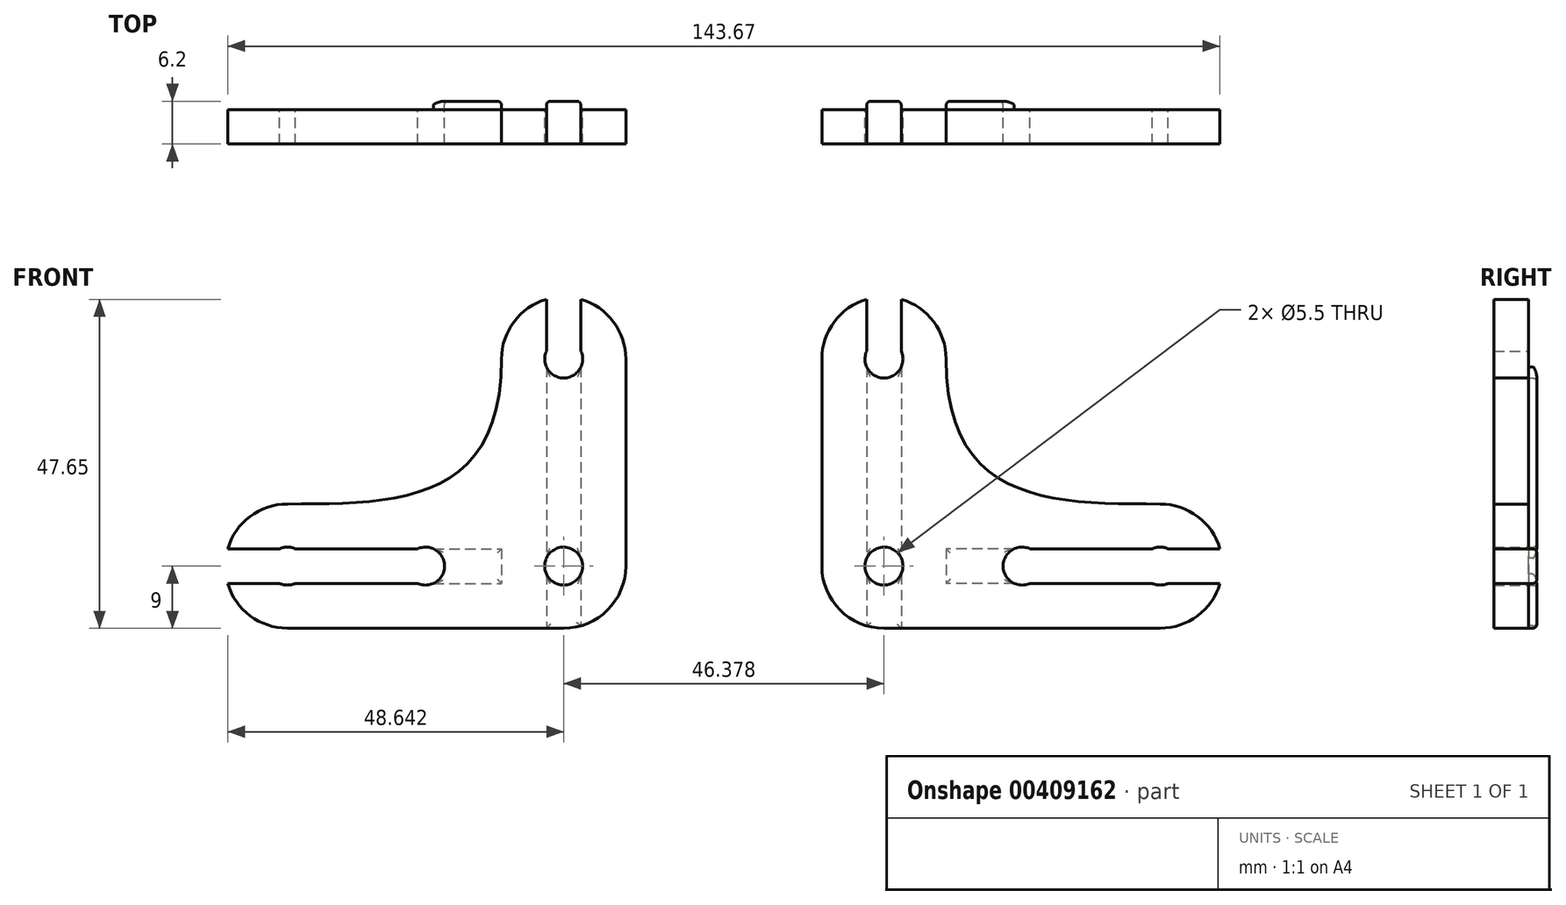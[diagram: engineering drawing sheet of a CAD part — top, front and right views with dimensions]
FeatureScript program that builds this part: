
annotation { "Feature Type Name" : "Feature", "Feature Type Description" : "" }
export const myFeature = defineFeature(function(context is Context, id is Id, definition is map)
    precondition{}
    {
        {
            var Q0;
            Q0=qCreatedBy(makeId("Front.planeOp"),FACE);
            var sketch = newSketch(context, id + "F0", { "sketchPlane" : qUnion([Q0])});
            skLineSegment(sketch, "E0.left", {"start": v(-18, 0) * mm, "end": v(-18, 30) * mm});
            skArc(sketch, "E1", {"start": v(-18, 30) * mm, "mid": v(-9, 39) * mm, "end": v(0, 30) * mm});
            skArc(sketch, "E2", {"start": v(31, 9) * mm, "mid": v(37.36, 6.36) * mm, "end": v(40, 0) * mm});
            skLineSegment(sketch, "E3", {"start": v(0, 30) * mm, "end": v(0, 9) * mm, "construction": true});
            skLineSegment(sketch, "E4", {"start": v(0, 9) * mm, "end": v(31, 9) * mm, "construction": true});
            skLineSegment(sketch, "E5", {"start": v(-18, 39) * mm, "end": v(0, 39) * mm, "construction": true});
            skFitSpline(sketch, "E6", {"points": [v(0, 30) * mm, v(31, 9) * mm], "startDerivative": vector(0, -63) * mm, "endDerivative": vector(46.5, 0) * mm});
            skCircle(sketch, "E7", {"center": v(-9, 30) * mm, "radius": 2.75 * mm});
            skCircle(sketch, "E8", {"center": v(-9, 0) * mm, "radius": 2.75 * mm});
            skCircle(sketch, "E9", {"center": v(31, 0) * mm, "radius": 2.75 * mm});
            skCircle(sketch, "E10", {"center": v(11, 0) * mm, "radius": 2.75 * mm});
            skLineSegment(sketch, "E11.MirrorCS", {"start": v(-18, 0) * mm, "end": v(-18, 0) * mm});
            skArc(sketch, "E12.MirrorCS", {"start": v(31, -9) * mm, "mid": v(37.36, -6.36) * mm, "end": v(40, 0) * mm});
            skCircle(sketch, "E13", {"center": v(-9, 30) * mm, "radius": 2.5 * mm, "construction": true});
            skCircle(sketch, "E14", {"center": v(31, 0) * mm, "radius": 2.5 * mm, "construction": true});
            skLineSegment(sketch, "E15.left", {"start": v(-6.5, 38.65) * mm, "end": v(-6.5, -9) * mm});
            skLineSegment(sketch, "E16.bottom", {"start": v(39.65, 2.5) * mm, "end": v(0, 2.5) * mm});
            skLineSegment(sketch, "E16.top", {"start": v(39.65, -2.5) * mm, "end": v(0, -2.5) * mm});
            skLineSegment(sketch, "E16.right", {"start": v(0, 2.5) * mm, "end": v(0, -2.5) * mm});
            skPoint(sketch, "E16.middle", {"position": v(19.82, 0) * mm});
            skLineSegment(sketch, "E17", {"start": v(31, -9) * mm, "end": v(-9, -9) * mm});
            skPoint(sketch, "E18.orphan", {"position": v(-11.5, -38.65) * mm});
            skPoint(sketch, "E19.orphan", {"position": v(-6.5, -38.65) * mm});
            skArc(sketch, "E20.filletArc", {"start": v(-18, 0) * mm, "mid": v(-15.36, -6.36) * mm, "end": v(-9, -9) * mm});
            skLineSegment(sketch, "E21", {"start": v(-11.5, 38.65) * mm, "end": v(-11.5, -8.65) * mm});
            skLineSegment(sketch, "E22", {"start": v(-32.19, 44.68) * mm, "end": v(-32.19, -13.7) * mm});
            skSolve(sketch);
        }
        {
            var Q0;
            {var subQ0=sQuery(id+"F0.wireOp",EDGE,"E15.right");var subQ1=sQuery(id+"F0.wireOp",EDGE,"E8");var subQ2=makeQuery(id+"F0.imprint","INTERSECT",VERTEX,{"disambiguationData":[OD(1.0)],"derivedFrom":[subQ1,subQ0]});Q0=makeQuery(id+"F0.imprint","IMPRINT",FACE,{"disambiguationData":[TD([[makeQuery(id+"F0.imprint","IMPRINT",EDGE,{"disambiguationData":[TD([[subQ2,-1.0]])],"derivedFrom":subQ1}),-1.0]])]});}
            var Q1;
            {var subQ12=sQuery(id+"F0.wireOp",EDGE,"E0.left");Q1=makeQuery(id+"F0.imprint","IMPRINT",FACE,{"disambiguationData":[TD([[makeQuery(id+"F0.imprint","IMPRINT",EDGE,{"derivedFrom":subQ12}),-1.0]])]});}
            var Q2;
            {var subQ0=sQuery(id+"F0.wireOp",EDGE,"E16.bottom");var subQ1=sQuery(id+"F0.wireOp",EDGE,"E9");var subQ2=makeQuery(id+"F0.imprint","INTERSECT",VERTEX,{"disambiguationData":[OD(0.0)],"derivedFrom":[subQ1,subQ0]});Q2=makeQuery(id+"F0.imprint","IMPRINT",FACE,{"disambiguationData":[TD([[makeQuery(id+"F0.imprint","IMPRINT",EDGE,{"disambiguationData":[TD([[subQ2,-1.0]])],"derivedFrom":subQ1}),-1.0]])]});}
            var Q3;
            {var subQ0=sQuery(id+"F0.wireOp",EDGE,"E15.right");var subQ1=sQuery(id+"F0.wireOp",EDGE,"807e0331-1f37-435d-b5e4-c923ac2277230.MirrorC");var subQ2=makeQuery(id+"F0.imprint","INTERSECT",VERTEX,{"disambiguationData":[OD(0.0)],"derivedFrom":[subQ1,subQ0]});Q3=makeQuery(id+"F0.imprint","IMPRINT",FACE,{"disambiguationData":[TD([[makeQuery(id+"F0.imprint","IMPRINT",EDGE,{"disambiguationData":[TD([[subQ2,1.0]])],"derivedFrom":subQ1}),-1.0]])]});}
            var Q4;
            {var subQ0=sQuery(id+"F0.wireOp",EDGE,"E15.right");var subQ1=sQuery(id+"F0.wireOp",EDGE,"E7");var subQ2=makeQuery(id+"F0.imprint","INTERSECT",VERTEX,{"disambiguationData":[OD(0.0)],"derivedFrom":[subQ1,subQ0]});Q4=makeQuery(id+"F0.imprint","IMPRINT",FACE,{"disambiguationData":[TD([[makeQuery(id+"F0.imprint","IMPRINT",EDGE,{"disambiguationData":[TD([[subQ2,1.0]])],"derivedFrom":subQ1}),1.0]])]});}
            var Q5;
            {var subQ0=sQuery(id+"F0.wireOp",EDGE,"E15.right");var subQ1=sQuery(id+"F0.wireOp",EDGE,"E8");var subQ2=makeQuery(id+"F0.imprint","INTERSECT",VERTEX,{"disambiguationData":[OD(0.0)],"derivedFrom":[subQ1,subQ0]});Q5=makeQuery(id+"F0.imprint","IMPRINT",FACE,{"disambiguationData":[TD([[makeQuery(id+"F0.imprint","IMPRINT",EDGE,{"disambiguationData":[TD([[subQ2,1.0]])],"derivedFrom":subQ1}),1.0]])]});}
            var Q6;
            {var subQ0=sQuery(id+"F0.wireOp",EDGE,"E15.right");var subQ1=sQuery(id+"F0.wireOp",EDGE,"E7");var subQ2=makeQuery(id+"F0.imprint","INTERSECT",VERTEX,{"disambiguationData":[OD(1.0)],"derivedFrom":[subQ1,subQ0]});Q6=makeQuery(id+"F0.imprint","IMPRINT",FACE,{"disambiguationData":[TD([[makeQuery(id+"F0.imprint","IMPRINT",EDGE,{"disambiguationData":[TD([[subQ2,-1.0]])],"derivedFrom":subQ1}),-1.0]])]});}
            var Q7;
            {var subQ5=sQuery(id+"F0.wireOp",EDGE,"E16.right");Q7=makeQuery(id+"F0.imprint","IMPRINT",FACE,{"disambiguationData":[TD([[makeQuery(id+"F0.imprint","IMPRINT",EDGE,{"derivedFrom":subQ5}),1.0]])]});}
            var Q8;
            {var subQ0=sQuery(id+"F0.wireOp",EDGE,"E15.right");var subQ1=sQuery(id+"F0.wireOp",EDGE,"E8");var subQ2=makeQuery(id+"F0.imprint","INTERSECT",VERTEX,{"disambiguationData":[OD(0.0)],"derivedFrom":[subQ1,subQ0]});Q8=makeQuery(id+"F0.imprint","IMPRINT",FACE,{"disambiguationData":[TD([[makeQuery(id+"F0.imprint","IMPRINT",EDGE,{"disambiguationData":[TD([[subQ2,-1.0]])],"derivedFrom":subQ1}),1.0]])]});}
            var Q9;
            {var subQ0=sQuery(id+"F0.wireOp",EDGE,"E15.left");var subQ1=sQuery(id+"F0.wireOp",EDGE,"62d9e975-9eb4-4a92-8864-7b3c9c0b367b0.MirrorCS");var subQ2=makeQuery(id+"F0.imprint","INTERSECT",VERTEX,{"derivedFrom":[subQ1,subQ0]});Q9=makeQuery(id+"F0.imprint","IMPRINT",FACE,{"disambiguationData":[TD([[makeQuery(id+"F0.imprint","IMPRINT",EDGE,{"disambiguationData":[TD([[subQ2,1.0]])],"derivedFrom":subQ1}),1.0]])]});}
            var Q10;
            {var subQ21=sQuery(id+"F0.wireOp",EDGE,"E6");Q10=makeQuery(id+"F0.imprint","IMPRINT",FACE,{"disambiguationData":[TD([[makeQuery(id+"F0.imprint","IMPRINT",EDGE,{"derivedFrom":subQ21}),-1.0]])]});}
            var Q11;
            {var subQ1=sQuery(id+"F0.wireOp",EDGE,"E2");var subQ5=sQuery(id+"F0.wireOp",EDGE,"E12.MirrorCS");var subQ6=makeQuery(id+"F0.imprint","INTERSECT",VERTEX,{"derivedFrom":[subQ1,subQ5]});Q11=makeQuery(id+"F0.imprint","IMPRINT",FACE,{"disambiguationData":[TD([[makeQuery(id+"F0.imprint","IMPRINT",EDGE,{"disambiguationData":[TD([[subQ6,1.0]])],"derivedFrom":subQ1}),-1.0]])]});}
            var Q12;
            {var subQ0=sQuery(id+"F0.wireOp",EDGE,"E15.left");var subQ1=sQuery(id+"F0.wireOp",EDGE,"E1");var subQ2=makeQuery(id+"F0.imprint","INTERSECT",VERTEX,{"derivedFrom":[subQ1,subQ0]});Q12=makeQuery(id+"F0.imprint","IMPRINT",FACE,{"disambiguationData":[TD([[makeQuery(id+"F0.imprint","IMPRINT",EDGE,{"disambiguationData":[TD([[subQ2,1.0]])],"derivedFrom":subQ1}),-1.0]])]});}
            var Q13;
            {var subQ0=sQuery(id+"F0.wireOp",EDGE,"E15.left");var subQ1=sQuery(id+"F0.wireOp",EDGE,"807e0331-1f37-435d-b5e4-c923ac2277230.MirrorC");var subQ2=makeQuery(id+"F0.imprint","INTERSECT",VERTEX,{"disambiguationData":[OD(0.0)],"derivedFrom":[subQ1,subQ0]});Q13=makeQuery(id+"F0.imprint","IMPRINT",FACE,{"disambiguationData":[TD([[makeQuery(id+"F0.imprint","IMPRINT",EDGE,{"disambiguationData":[TD([[subQ2,1.0]])],"derivedFrom":subQ1}),-1.0]])]});}
            var Q14;
            {var subQ0=sQuery(id+"F0.wireOp",EDGE,"E15.right");var subQ1=sQuery(id+"F0.wireOp",EDGE,"E7");var subQ2=makeQuery(id+"F0.imprint","INTERSECT",VERTEX,{"disambiguationData":[OD(0.0)],"derivedFrom":[subQ1,subQ0]});Q14=makeQuery(id+"F0.imprint","IMPRINT",FACE,{"disambiguationData":[TD([[makeQuery(id+"F0.imprint","IMPRINT",EDGE,{"disambiguationData":[TD([[subQ2,-1.0]])],"derivedFrom":subQ1}),1.0]])]});}
            var Q15;
            {var subQ0=sQuery(id+"F0.wireOp",EDGE,"E15.right");var subQ1=sQuery(id+"F0.wireOp",EDGE,"807e0331-1f37-435d-b5e4-c923ac2277230.MirrorC");var subQ2=makeQuery(id+"F0.imprint","INTERSECT",VERTEX,{"disambiguationData":[OD(0.0)],"derivedFrom":[subQ1,subQ0]});Q15=makeQuery(id+"F0.imprint","IMPRINT",FACE,{"disambiguationData":[TD([[makeQuery(id+"F0.imprint","IMPRINT",EDGE,{"disambiguationData":[TD([[subQ2,-1.0]])],"derivedFrom":subQ1}),-1.0]])]});}
            var Q16;
            {var subQ0=sQuery(id+"F0.wireOp",EDGE,"E21");var subQ1=sQuery(id+"F0.wireOp",EDGE,"E7");var subQ2=makeQuery(id+"F0.imprint","INTERSECT",VERTEX,{"disambiguationData":[OD(1.0)],"derivedFrom":[subQ1,subQ0]});Q16=makeQuery(id+"F0.imprint","IMPRINT",FACE,{"disambiguationData":[TD([[makeQuery(id+"F0.imprint","IMPRINT",EDGE,{"disambiguationData":[TD([[subQ2,-1.0]])],"derivedFrom":subQ1}),-1.0]])]});}
            var Q17;
            {var subQ5=sQuery(id+"F0.wireOp",EDGE,"E21");var subQ7=sQuery(id+"F0.wireOp",EDGE,"E8");var subQ9=makeQuery(id+"F0.imprint","INTERSECT",VERTEX,{"disambiguationData":[OD(1.0)],"derivedFrom":[subQ7,subQ5]});Q17=makeQuery(id+"F0.imprint","IMPRINT",FACE,{"disambiguationData":[TD([[makeQuery(id+"F0.imprint","IMPRINT",EDGE,{"disambiguationData":[TD([[subQ9,-1.0]])],"derivedFrom":subQ7}),-1.0]])]});}
            extrude(context, id + "F1", {"entities" : qUnion([Q0, Q1, Q2, Q3, Q4, Q5, Q6, Q7, Q8, Q9, Q10, Q11, Q12, Q13, Q14, Q15, Q16, Q17]), "depth" : 5 * mm, "offsetDistance" : 25 * mm});
        }
        {
            var Q0;
            {var subQ3=sQuery(id+"F0.wireOp",EDGE,"E8");var subQ6=sQuery(id+"F0.wireOp",EDGE,"E15.right");var subQ8=makeQuery(id+"F0.imprint","INTERSECT",VERTEX,{"disambiguationData":[OD(1.0)],"derivedFrom":[subQ3,subQ6]});Q0=makeQuery(id+"F0.imprint","IMPRINT",FACE,{"disambiguationData":[TD([[makeQuery(id+"F0.imprint","IMPRINT",EDGE,{"disambiguationData":[TD([[subQ8,-1.0]])],"derivedFrom":subQ3}),-1.0]])]});}
            var Q1;
            {var subQ3=sQuery(id+"F0.wireOp",EDGE,"E8");var subQ6=sQuery(id+"F0.wireOp",EDGE,"E15.right");var subQ8=makeQuery(id+"F0.imprint","INTERSECT",VERTEX,{"disambiguationData":[OD(0.0)],"derivedFrom":[subQ3,subQ6]});Q1=makeQuery(id+"F0.imprint","IMPRINT",FACE,{"disambiguationData":[TD([[makeQuery(id+"F0.imprint","IMPRINT",EDGE,{"disambiguationData":[TD([[subQ8,1.0]])],"derivedFrom":subQ3}),-1.0]])]});}
            var Q2;
            {var subQ5=sQuery(id+"F0.wireOp",EDGE,"E16.right");Q2=makeQuery(id+"F0.imprint","IMPRINT",FACE,{"disambiguationData":[TD([[makeQuery(id+"F0.imprint","IMPRINT",EDGE,{"derivedFrom":subQ5}),1.0]])]});}
            var Q3;
            {var subQ1=sQuery(id+"F0.wireOp",EDGE,"E16.bottom");var subQ4=sQuery(id+"F0.wireOp",EDGE,"E10");var subQ5=makeQuery(id+"F0.imprint","INTERSECT",VERTEX,{"disambiguationData":[OD(1.0)],"derivedFrom":[subQ4,subQ1]});Q3=makeQuery(id+"F0.imprint","IMPRINT",FACE,{"disambiguationData":[TD([[makeQuery(id+"F0.imprint","IMPRINT",EDGE,{"disambiguationData":[TD([[subQ5,1.0]])],"derivedFrom":subQ4}),-1.0]])]});}
            var Q4;
            {var subQ1=sQuery(id+"F0.wireOp",EDGE,"E2");var subQ5=sQuery(id+"F0.wireOp",EDGE,"E12.MirrorCS");var subQ6=makeQuery(id+"F0.imprint","INTERSECT",VERTEX,{"derivedFrom":[subQ1,subQ5]});Q4=makeQuery(id+"F0.imprint","IMPRINT",FACE,{"disambiguationData":[TD([[makeQuery(id+"F0.imprint","IMPRINT",EDGE,{"disambiguationData":[TD([[subQ6,1.0]])],"derivedFrom":subQ1}),-1.0]])]});}
            var Q5;
            {var subQ0=sQuery(id+"F0.wireOp",EDGE,"E15.left");var subQ1=sQuery(id+"F0.wireOp",EDGE,"E1");var subQ2=makeQuery(id+"F0.imprint","INTERSECT",VERTEX,{"derivedFrom":[subQ1,subQ0]});Q5=makeQuery(id+"F0.imprint","IMPRINT",FACE,{"disambiguationData":[TD([[makeQuery(id+"F0.imprint","IMPRINT",EDGE,{"disambiguationData":[TD([[subQ2,1.0]])],"derivedFrom":subQ1}),-1.0]])]});}
            var Q6;
            {var subQ0=sQuery(id+"F0.wireOp",EDGE,"E15.left");var subQ1=sQuery(id+"F0.wireOp",EDGE,"62d9e975-9eb4-4a92-8864-7b3c9c0b367b0.MirrorCS");var subQ2=makeQuery(id+"F0.imprint","INTERSECT",VERTEX,{"derivedFrom":[subQ1,subQ0]});Q6=makeQuery(id+"F0.imprint","IMPRINT",FACE,{"disambiguationData":[TD([[makeQuery(id+"F0.imprint","IMPRINT",EDGE,{"disambiguationData":[TD([[subQ2,1.0]])],"derivedFrom":subQ1}),1.0]])]});}
            var Q7;
            {var subQ0=sQuery(id+"F0.wireOp",EDGE,"E21");var subQ1=sQuery(id+"F0.wireOp",EDGE,"E7");var subQ2=makeQuery(id+"F0.imprint","INTERSECT",VERTEX,{"disambiguationData":[OD(1.0)],"derivedFrom":[subQ1,subQ0]});Q7=makeQuery(id+"F0.imprint","IMPRINT",FACE,{"disambiguationData":[TD([[makeQuery(id+"F0.imprint","IMPRINT",EDGE,{"disambiguationData":[TD([[subQ2,-1.0]])],"derivedFrom":subQ1}),-1.0]])]});}
            var Q8;
            {var subQ5=sQuery(id+"F0.wireOp",EDGE,"E21");var subQ7=sQuery(id+"F0.wireOp",EDGE,"E8");var subQ9=makeQuery(id+"F0.imprint","INTERSECT",VERTEX,{"disambiguationData":[OD(1.0)],"derivedFrom":[subQ7,subQ5]});Q8=makeQuery(id+"F0.imprint","IMPRINT",FACE,{"disambiguationData":[TD([[makeQuery(id+"F0.imprint","IMPRINT",EDGE,{"disambiguationData":[TD([[subQ9,-1.0]])],"derivedFrom":subQ7}),-1.0]])]});}
            extrude(context, id + "F2", {"entities" : qUnion([Q0, Q1, Q2, Q3, Q4, Q5, Q6, Q7, Q8]), "operationType" : NewBodyOperationType.ADD, "oppositeDirection" : true, "depth" : 1.2 * mm, "offsetDistance" : 25 * mm});
        }
        {
            var Q0;
            Q0=makeQuery(id+"F2.opExtrude","CAP_FACE",FACE,{"disambiguationData":[OSD([sQuery(id+"F0.wireOp",EDGE,"E8"),sQuery(id+"F0.wireOp",EDGE,"807e0331-1f37-435d-b5e4-c923ac2277230.MirrorC"),sQuery(id+"F0.wireOp",EDGE,"E15.left"),sQuery(id+"F0.wireOp",EDGE,"E15.right")])],"isStart":false});
            var Q1;
            Q1=makeQuery(id+"F2.opExtrude","CAP_FACE",FACE,{"disambiguationData":[OSD([sQuery(id+"F0.wireOp",EDGE,"62d9e975-9eb4-4a92-8864-7b3c9c0b367b0.MirrorCS"),sQuery(id+"F0.wireOp",EDGE,"807e0331-1f37-435d-b5e4-c923ac2277230.MirrorC"),sQuery(id+"F0.wireOp",EDGE,"E15.left"),sQuery(id+"F0.wireOp",EDGE,"E15.right")])],"isStart":false});
            var Q2;
            Q2=makeQuery(id+"F2.opExtrude","CAP_FACE",FACE,{"disambiguationData":[OSD([sQuery(id+"F0.wireOp",EDGE,"E7"),sQuery(id+"F0.wireOp",EDGE,"E8"),sQuery(id+"F0.wireOp",EDGE,"E15.left"),sQuery(id+"F0.wireOp",EDGE,"E15.right")])],"isStart":false});
            var Q3;
            Q3=makeQuery(id+"F2.opExtrude","CAP_FACE",FACE,{"disambiguationData":[OSD([sQuery(id+"F0.wireOp",EDGE,"E1"),sQuery(id+"F0.wireOp",EDGE,"E7"),sQuery(id+"F0.wireOp",EDGE,"E15.left"),sQuery(id+"F0.wireOp",EDGE,"E15.right")])],"isStart":false});
            var Q4;
            Q4=makeQuery(id+"F2.opExtrude","CAP_FACE",FACE,{"disambiguationData":[OSD([sQuery(id+"F0.wireOp",EDGE,"E10"),sQuery(id+"F0.wireOp",EDGE,"E16.bottom"),sQuery(id+"F0.wireOp",EDGE,"E16.top"),sQuery(id+"F0.wireOp",EDGE,"E16.right")])],"isStart":false});
            var Q5;
            Q5=makeQuery(id+"F2.opExtrude","CAP_FACE",FACE,{"disambiguationData":[OSD([sQuery(id+"F0.wireOp",EDGE,"E9"),sQuery(id+"F0.wireOp",EDGE,"E10"),sQuery(id+"F0.wireOp",EDGE,"E16.bottom"),sQuery(id+"F0.wireOp",EDGE,"E16.top")])],"isStart":false});
            var Q6;
            Q6=makeQuery(id+"F2.opExtrude","CAP_FACE",FACE,{"disambiguationData":[OSD([sQuery(id+"F0.wireOp",EDGE,"E2"),sQuery(id+"F0.wireOp",EDGE,"E9"),sQuery(id+"F0.wireOp",EDGE,"E12.MirrorCS"),sQuery(id+"F0.wireOp",EDGE,"E16.bottom"),sQuery(id+"F0.wireOp",EDGE,"E16.top")])],"isStart":false});
            var Q7;
            Q7=makeQuery(id+"F2.opExtrude","CAP_FACE",FACE,{"disambiguationData":[OSD([sQuery(id+"F0.wireOp",EDGE,"E8"),sQuery(id+"F0.wireOp",EDGE,"E15.left"),sQuery(id+"F0.wireOp",EDGE,"E17"),sQuery(id+"F0.wireOp",EDGE,"E20.filletArc"),sQuery(id+"F0.wireOp",EDGE,"E21")])],"isStart":false});
            var Q8;
            {var subQ0=sQuery(id+"F0.wireOp",EDGE,"E16.top");Q8=makeQuery(id+"F2.opExtrude","CAP_EDGE",EDGE,{"disambiguationData":[OSD([subQ0]),TDD([makeQuery(id+"F0.imprint","IMPRINT",EDGE,{"disambiguationData":[TD([[makeQuery(id+"F0.imprint","INTERSECT",VERTEX,{"derivedFrom":[subQ0,sQuery(id+"F0.wireOp",EDGE,"E16.right")]}),1.0]])],"derivedFrom":subQ0})])],"isStart":true});}
            var Q9;
            {var subQ0=sQuery(id+"F0.wireOp",EDGE,"E21");Q9=makeQuery(id+"F2.opExtrude","CAP_EDGE",EDGE,{"disambiguationData":[OSD([subQ0]),TDD([makeQuery(id+"F0.imprint","IMPRINT",EDGE,{"disambiguationData":[TD([[makeQuery(id+"F0.imprint","INTERSECT",VERTEX,{"disambiguationData":[OD(1.0)],"derivedFrom":[sQuery(id+"F0.wireOp",EDGE,"E7"),subQ0]}),-1.0]])],"derivedFrom":subQ0})])],"isStart":true});}
            var Q10;
            {var subQ0=sQuery(id+"F0.wireOp",EDGE,"E16.bottom");Q10=makeQuery(id+"F2.opExtrude","CAP_EDGE",EDGE,{"disambiguationData":[OSD([subQ0]),TDD([makeQuery(id+"F0.imprint","IMPRINT",EDGE,{"disambiguationData":[TD([[makeQuery(id+"F0.imprint","INTERSECT",VERTEX,{"derivedFrom":[subQ0,sQuery(id+"F0.wireOp",EDGE,"E16.right")]}),1.0]])],"derivedFrom":subQ0})])],"isStart":true});}
            var Q11;
            {var subQ0=sQuery(id+"F0.wireOp",EDGE,"E15.left");Q11=makeQuery(id+"F2.opExtrude","CAP_EDGE",EDGE,{"disambiguationData":[OSD([subQ0]),TDD([makeQuery(id+"F0.imprint","IMPRINT",EDGE,{"disambiguationData":[TD([[makeQuery(id+"F0.imprint","INTERSECT",VERTEX,{"disambiguationData":[OD(1.0)],"derivedFrom":[sQuery(id+"F0.wireOp",EDGE,"E7"),subQ0]}),-1.0]])],"derivedFrom":subQ0})])],"isStart":true});}
            fillet(context, id + "F3", {"entities" : qUnion([Q0, Q1, Q2, Q3, Q4, Q5, Q6, Q7, Q8, Q9, Q10, Q11]), "radius" : 0.6 * mm, "tangentPropagation" : true, "allowEdgeOverflow" : false});
        }
        {
            var Q0;
            Q0=sQuery(id+"F0.wireOp",EDGE,"E22");
            extrude(context, id + "F4", {"bodyType" : ExtendedToolBodyType.SURFACE, "surfaceEntities" : qUnion([Q0]), "depth" : 25 * mm, "offsetDistance" : 25 * mm});
        }
        {
            var Q0;
            Q0=makeQuery(id+"F1.opExtrude","SWEPT_BODY",BODY,{"disambiguationData":[OSD([sQuery(id+"F0.wireOp",EDGE,"E0.left"),sQuery(id+"F0.wireOp",EDGE,"E1"),sQuery(id+"F0.wireOp",EDGE,"E2"),sQuery(id+"F0.wireOp",EDGE,"E6"),sQuery(id+"F0.wireOp",EDGE,"E7"),sQuery(id+"F0.wireOp",EDGE,"E8"),sQuery(id+"F0.wireOp",EDGE,"E9"),sQuery(id+"F0.wireOp",EDGE,"E10"),sQuery(id+"F0.wireOp",EDGE,"E12.MirrorCS"),sQuery(id+"F0.wireOp",EDGE,"E17"),sQuery(id+"F0.wireOp",EDGE,"E20.filletArc")])]});
            var Q1;
            Q1=makeQuery(id+"F4.opExtrude","SWEPT_FACE",FACE,{"disambiguationData":[OSD([sQuery(id+"F0.wireOp",EDGE,"E22")])]});
            mirror(context, id + "F5", {"entities" : qUnion([Q0]), "mirrorPlane" : qUnion([Q1])});
        }
        {
            var Q0;
            Q0=makeQuery(id+"F4.opExtrude","SWEPT_BODY",BODY,{"disambiguationData":[OSD([sQuery(id+"F0.wireOp",EDGE,"E22")])]});
            deleteBodies(context, id + "F6", {"entities" : qUnion([Q0])});
        }
    });
